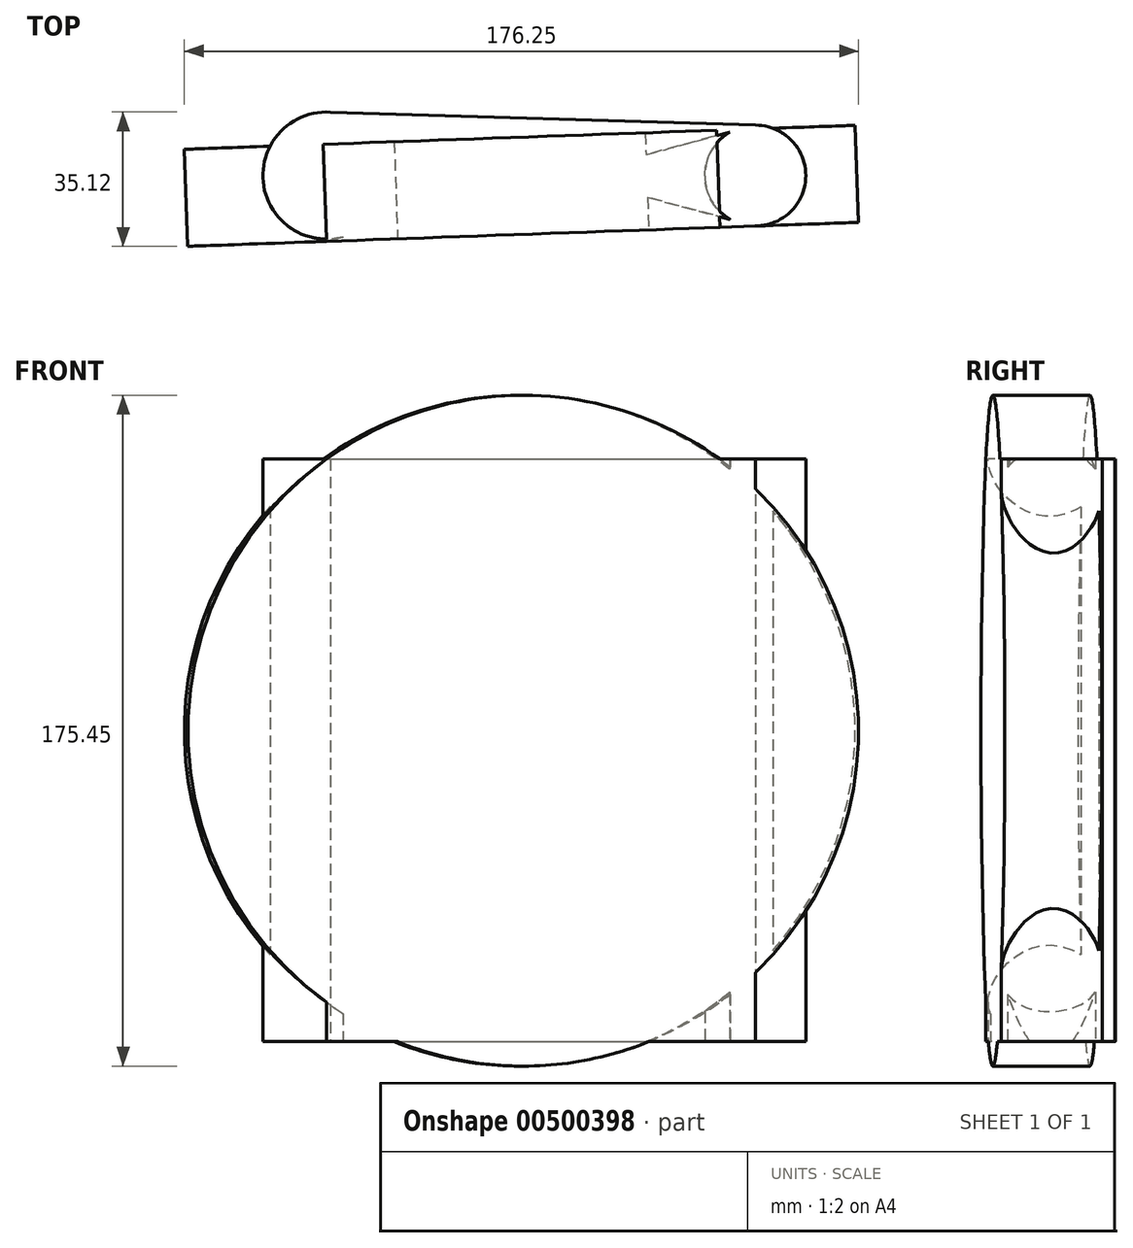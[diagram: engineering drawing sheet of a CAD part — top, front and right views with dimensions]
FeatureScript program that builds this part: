
annotation { "Feature Type Name" : "Feature", "Feature Type Description" : "" }
export const myFeature = defineFeature(function(context is Context, id is Id, definition is map)
    precondition{}
    {
        {
            var Q0;
            Q0=qCreatedBy(makeId("Top.planeOp"),FACE);
            var sketch = newSketch(context, id + "F0", { "sketchPlane" : qUnion([Q0])});
            skCircle(sketch, "E0", {"center": v(0, 0) * mm, "radius": 16.61 * mm});
            skCircle(sketch, "E1", {"center": v(112.13, 0) * mm, "radius": 13.2 * mm});
            skLineSegment(sketch, "E2", {"start": v(0, 16.61) * mm, "end": v(112.13, 13.2) * mm});
            skLineSegment(sketch, "E3", {"start": v(112.13, 13.2) * mm, "end": v(0, -17.21) * mm});
            skLineSegment(sketch, "E4", {"start": v(0, -17.21) * mm, "end": v(112.13, -13.2) * mm});
            skLineSegment(sketch, "E5", {"start": v(112.13, -13.2) * mm, "end": v(0, 16.61) * mm});
            skSolve(sketch);
        }
        {
            var Q0;
            Q0 = qSketchRegion(id + "F0", true);
            extrude(context, id + "F1", {"entities" : qUnion([Q0]), "depth" : 152.4 * mm});
        }
        {
            var Q0;
            Q0=makeQuery(id+"F1.opExtrude","SWEPT_FACE",FACE,{"disambiguationData":[OSD([sQuery(id+"F0.wireOp",EDGE,"E4")])]});
            var sketch = newSketch(context, id + "F2", { "sketchPlane" : qUnion([Q0])});
            skCircle(sketch, "E6", {"center": v(50.86, 81.35) * mm, "radius": 87.73 * mm});
            skSolve(sketch);
        }
        {
            var Q0;
            Q0 = qSketchRegion(id + "F2", true);
            extrude(context, id + "F3", {"entities" : qUnion([Q0]), "operationType" : NewBodyOperationType.ADD, "oppositeDirection" : true, "depth" : 25.4 * mm});
        }
    });
